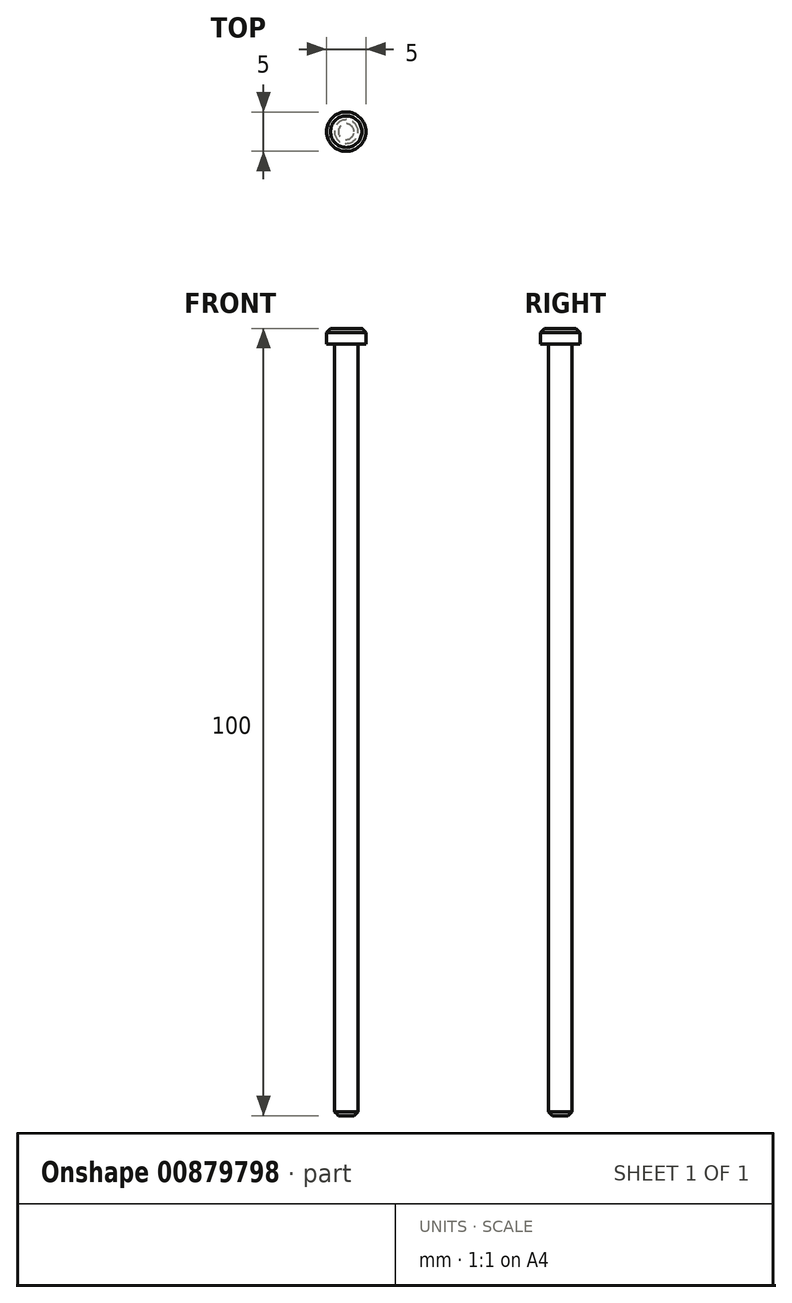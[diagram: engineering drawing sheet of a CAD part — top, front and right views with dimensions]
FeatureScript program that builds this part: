
annotation { "Feature Type Name" : "Feature", "Feature Type Description" : "" }
export const myFeature = defineFeature(function(context is Context, id is Id, definition is map)
    precondition{}
    {
        {
            var Q0;
            Q0=qCreatedBy(makeId("Right.planeOp"),FACE);
            var sketch = newSketch(context, id + "F0", { "sketchPlane" : qUnion([Q0])});
            skLineSegment(sketch, "E0.bottom", {"start": v(-1.5, 49) * mm, "end": v(0, 49) * mm});
            skLineSegment(sketch, "E0.top", {"start": v(-1.5, -49) * mm, "end": v(0, -49) * mm});
            skLineSegment(sketch, "E0.left", {"start": v(-1.5, 49) * mm, "end": v(-1.5, -49) * mm});
            skLineSegment(sketch, "E0.right", {"start": v(0, 49) * mm, "end": v(0, -49) * mm});
            skSolve(sketch);
        }
        {
            var Q0;
            Q0=makeQuery(id+"F0.imprint","IMPRINT",FACE,{"disambiguationData":[TD([[makeQuery(id+"F0.imprint","IMPRINT",EDGE,{"derivedFrom":sQuery(id+"F0.wireOp",EDGE,"E0.bottom")}),-1.0]])]});
            var Q1;
            Q1=sQuery(id+"F0.wireOp",EDGE,"E0.right");
            revolve(context, id + "F1", {"surfaceOperationType" : NewSurfaceOperationType.NEW, "entities" : qUnion([Q0]), "axis" : qUnion([Q1]), "revolveType" : RevolveType.FULL});
        }
        {
            var Q0;
            Q0=makeQuery(id+"F1.opRevolve","SWEPT_EDGE",EDGE,{"disambiguationData":[OSD([sQuery(id+"F0.wireOp",EDGE,"E0.top"),sQuery(id+"F0.wireOp",EDGE,"E0.left")])]});
            chamfer(context, id + "F2", {"entities" : qUnion([Q0]), "width" : 0.5 * mm, "tangentPropagation" : true});
        }
        {
            var Q0;
            Q0=makeQuery(id+"F1.opRevolve","SWEPT_FACE",FACE,{"disambiguationData":[OSD([sQuery(id+"F0.wireOp",EDGE,"E0.bottom")])]});
            var sketch = newSketch(context, id + "F3", { "sketchPlane" : qUnion([Q0])});
            skCircle(sketch, "E1", {"center": v(0, 0) * mm, "radius": 2.5 * mm});
            skSolve(sketch);
        }
        {
            var Q0;
            Q0=makeQuery(id+"F3.imprint","IMPRINT",FACE,{"disambiguationData":[TD([[makeQuery(id+"F3.imprint","IMPRINT",EDGE,{"derivedFrom":sQuery(id+"F3.wireOp",EDGE,"E1")}),1.0]])]});
            var Q1;
            Q1=makeQuery(id+"F3.imprint","IMPRINT",FACE,{"disambiguationData":[TD([[makeQuery(id+"F3.imprint","IMPRINT",EDGE,{"derivedFrom":makeQuery(id+"F1.opRevolve","SWEPT_EDGE",EDGE,{"disambiguationData":[OSD([sQuery(id+"F0.wireOp",EDGE,"E0.bottom"),sQuery(id+"F0.wireOp",EDGE,"E0.left")])]})}),1.0]])]});
            extrude(context, id + "F4", {"entities" : qUnion([Q0, Q1]), "operationType" : NewBodyOperationType.ADD, "depth" : 2 * mm, "offsetDistance" : 25 * mm});
        }
        {
            var Q0;
            Q0=makeQuery(id+"F4.opExtrude","CAP_EDGE",EDGE,{"disambiguationData":[OSD([sQuery(id+"F3.wireOp",EDGE,"E1")])],"isStart":false});
            chamfer(context, id + "F5", {"entities" : qUnion([Q0]), "width" : 0.5 * mm, "tangentPropagation" : true});
        }
    });
